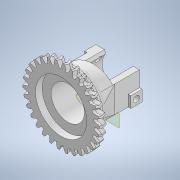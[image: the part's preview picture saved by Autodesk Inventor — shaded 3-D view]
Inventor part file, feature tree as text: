
AUTODESK INVENTOR PART (.ipt)
format: ipt  version: 2022 (Build 260153070, 153G)  size: 2,131,456 bytes
history: native  units: mm
features: sketch x8, extrude x8, mirror x3, fillet x3, loft x2, other x2, helix x1, pattern_circular x1, plane x1, chamfer x1
ambient origin geometry x8: Origin, YZ Plane, XZ Plane, XY Plane, X Axis, Y Axis, Z Axis, Center Point
bodies: Solid1 (feature_tree)
feature tree (30):
  sketch  "Sketch1"  dims[d0=1.5mm d1=0.0mm]
  extrude  "Extrusion1"  TaperAngle=0.0deg  [1 undecoded]
  helix  "Coil1"  [1 undecoded]
  pattern_circular  "Circular Pattern1"  [2 undecoded]
  mirror  "Mirror1"
  extrude  "Extrusion2"  Depth=12.0mm
  extrude  "Extrusion3"  Depth=12.0mm
  fillet  "Fillet1"  Radius=18.0mm
  fillet  "Fillet2"  Radius=5.0mm
  extrude  "Extrusion4"  Depth=12.0mm
  sketch  "Sketch5"  dims[d16=15.0mm]
  sketch  "Sketch6"  dims[d17=26.0mm]
  loft  "Loft1"
  extrude  "Extrusion5"  Depth=12.0mm
  extrude  "Extrusion6"  Depth=12.0mm
  mirror  "Mirror2"
  sketch  "Sketch9"  dims[d18=5.0mm d19=0.0mm]
  extrude  "Extrusion7"  Depth=12.0mm
  extrude  "Extrusion8"  TaperAngle=0.0deg  [1 undecoded]
  plane  "Work Plane1"
  loft  "Loft2"
  fillet  "Fillet3"  Radius=1.2mm
  mirror  "Mirror3"
  chamfer  "Chamfer1"  Distance=5.95mm
  sketch  "Sketch2"  dims[d2=275.559197mm d3=1.5mm d4=10.0mm d5=0.0mm d6=90.0deg d7=90.0deg d8=0.0mm d9=0.0mm d10=300.0mm d11=360.0deg]
  sketch  "Sketch3"  dims[d13=23.05mm]
  sketch  "Sketch4"  dims[d14=10.0mm d15=0.0mm]
  other  "Edges1"
  sketch  "Sketch11"  dims[d20=2.0mm d21=2.0mm d22=6.0mm d23=6.0mm d25=18.0mm d26=0.0mm d27=5.0mm d28=2.7mm d29=2.5mm d30=2.5mm d31=11.0mm d32=12.0mm d33=0.0mm d34=90.0deg d35=0.0mm d36=90.0deg d37=1.2mm d38=0.0mm d40=5.95mm d41=0.0mm d42=5.0mm d43=5.0mm d44=2.7mm d45=2.5mm d46=2.5mm d47=1.2mm d48=0.0mm d49=5.2mm d50=0.0mm d51=8.0mm d52=1.5mm d53=0.0mm d54=90.0deg d55=0.0mm d56=90.0deg d57=2.0mm d58=2.0mm d59=2.0mm d60=45.0deg]
  other  "Edges2"
note: 5 required parameter values undecoded (feature->parameter linkage not recoverable at this tier; creation-order binding heuristic only, values carry confidence <= 0.55)
